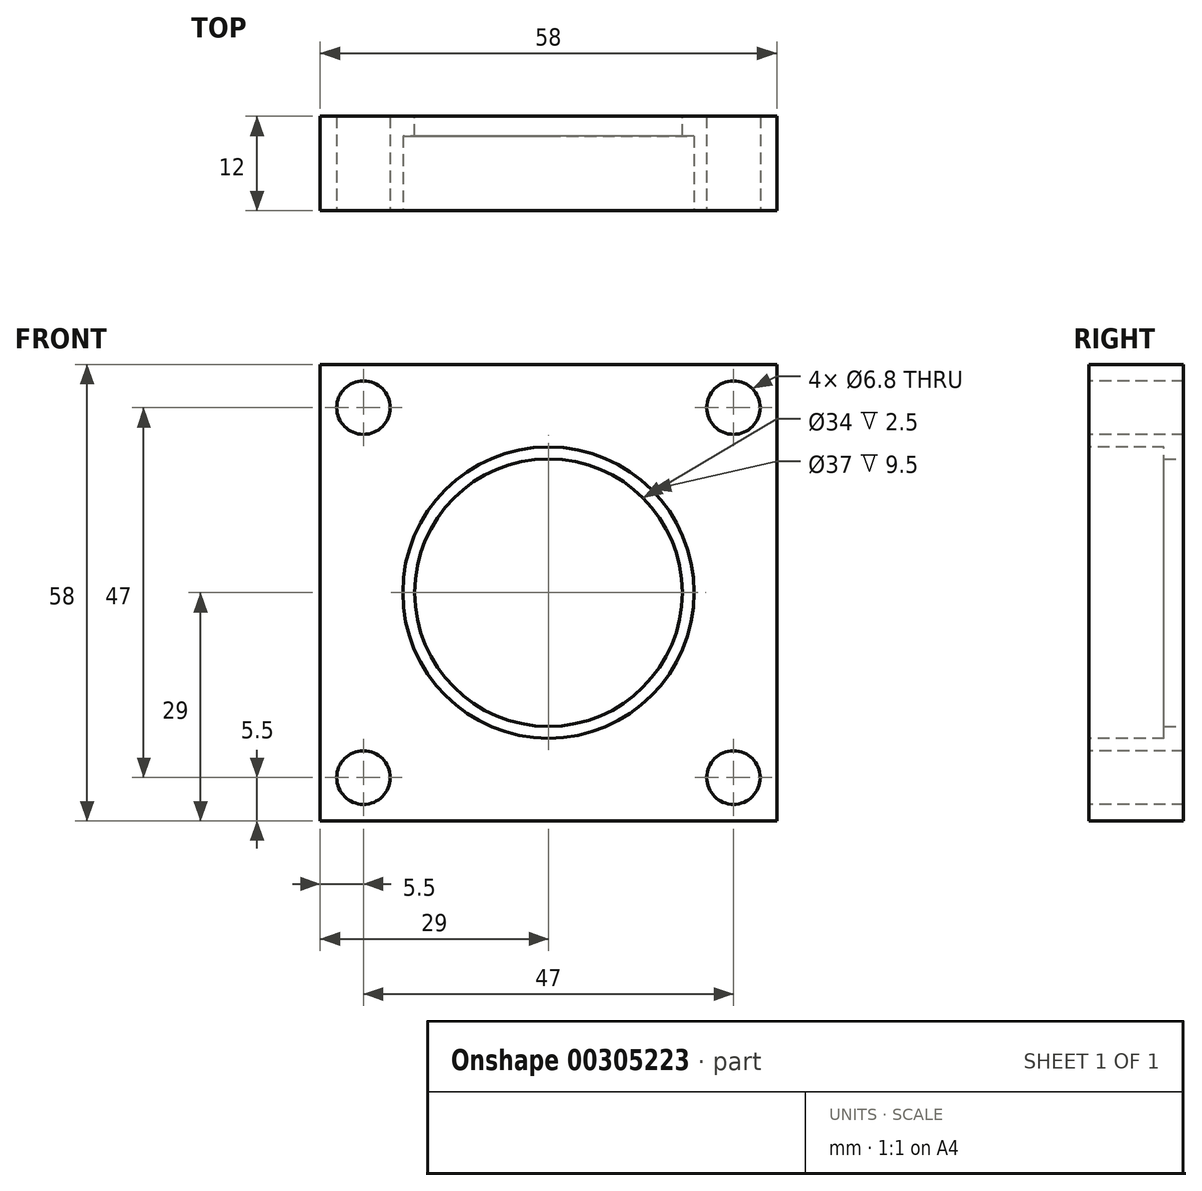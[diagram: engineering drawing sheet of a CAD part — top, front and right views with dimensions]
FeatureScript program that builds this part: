
annotation { "Feature Type Name" : "Feature", "Feature Type Description" : "" }
export const myFeature = defineFeature(function(context is Context, id is Id, definition is map)
    precondition{}
    {
        {
            var Q0;
            Q0=qCreatedBy(makeId("Front.planeOp"),FACE);
            var sketch = newSketch(context, id + "F0", { "sketchPlane" : qUnion([Q0])});
            skLineSegment(sketch, "E0.bottom", {"start": v(0, 0) * mm, "end": v(58, 0) * mm});
            skLineSegment(sketch, "E0.top", {"start": v(0, 58) * mm, "end": v(58, 58) * mm});
            skLineSegment(sketch, "E0.left", {"start": v(0, 0) * mm, "end": v(0, 58) * mm});
            skLineSegment(sketch, "E0.right", {"start": v(58, 0) * mm, "end": v(58, 58) * mm});
            skCircle(sketch, "E1", {"center": v(29, 29) * mm, "radius": 17 * mm});
            skSolve(sketch);
        }
        {
            var Q0;
            Q0=makeQuery(id+"F0.imprint","IMPRINT",FACE,{"disambiguationData":[TD([[makeQuery(id+"F0.imprint","IMPRINT",EDGE,{"derivedFrom":sQuery(id+"F0.wireOp",EDGE,"E0.bottom")}),1.0]])]});
            extrude(context, id + "F1", {"entities" : qUnion([Q0]), "depth" : 12 * mm});
        }
        {
            var Q0;
            Q0=makeQuery(id+"F1.opExtrude","CAP_FACE",FACE,{"disambiguationData":[OSD([sQuery(id+"F0.wireOp",EDGE,"E0.bottom"),sQuery(id+"F0.wireOp",EDGE,"E0.top"),sQuery(id+"F0.wireOp",EDGE,"E0.left"),sQuery(id+"F0.wireOp",EDGE,"E0.right"),sQuery(id+"F0.wireOp",EDGE,"E1")])],"isStart":false});
            var sketch = newSketch(context, id + "F2", { "sketchPlane" : qUnion([Q0])});
            skCircle(sketch, "E2", {"center": v(29, 29) * mm, "radius": 18.5 * mm});
            skSolve(sketch);
        }
        {
            var Q0;
            Q0=makeQuery(id+"F2.imprint","IMPRINT",FACE,{"disambiguationData":[TD([[makeQuery(id+"F2.imprint","IMPRINT",EDGE,{"derivedFrom":sQuery(id+"F2.wireOp",EDGE,"E2")}),1.0]])]});
            extrude(context, id + "F3", {"entities" : qUnion([Q0]), "operationType" : NewBodyOperationType.REMOVE, "oppositeDirection" : true, "depth" : 9.5 * mm});
        }
        {
            var Q0;
            Q0=makeQuery(id+"F2.imprint","IMPRINT",FACE,{"disambiguationData":[TD([[makeQuery(id+"F2.imprint","IMPRINT",EDGE,{"derivedFrom":sQuery(id+"F2.wireOp",EDGE,"E2")}),-1.0]])]});
            var sketch = newSketch(context, id + "F4", { "sketchPlane" : qUnion([Q0])});
            skPoint(sketch, "E3", {"position": v(5.5, 52.5) * mm});
            skPoint(sketch, "E4", {"position": v(5.5, 5.5) * mm});
            skPoint(sketch, "E5", {"position": v(52.5, 5.5) * mm});
            skPoint(sketch, "E6", {"position": v(52.5, 52.5) * mm});
            skSolve(sketch);
        }
        {
            var Q0;
            Q0=sQuery(id+"F4.wireOp",VERTEX,"E3");
            var Q1;
            Q1=sQuery(id+"F4.wireOp",VERTEX,"E6");
            var Q2;
            Q2=sQuery(id+"F4.wireOp",VERTEX,"E5");
            var Q3;
            Q3=sQuery(id+"F4.wireOp",VERTEX,"E4");
            var Q4;
            Q4=makeQuery(id+"F1.opExtrude","SWEPT_BODY",BODY,{"disambiguationData":[OSD([sQuery(id+"F0.wireOp",EDGE,"E0.bottom"),sQuery(id+"F0.wireOp",EDGE,"E0.top"),sQuery(id+"F0.wireOp",EDGE,"E0.left"),sQuery(id+"F0.wireOp",EDGE,"E0.right"),sQuery(id+"F0.wireOp",EDGE,"E1")])]});
            hole(context, id + "F5", {"style" : HoleStyle.SIMPLE, "endStyle" : HoleEndStyle.THROUGH, "holeDiameter" : 6.8 * mm, "tappedDepth" : 12 * mm, "tapClearance" : 3, "startFromSketch" : true, "locations" : qUnion([Q0, Q1, Q2, Q3]), "scope" : qUnion([Q4])});
        }
    });
